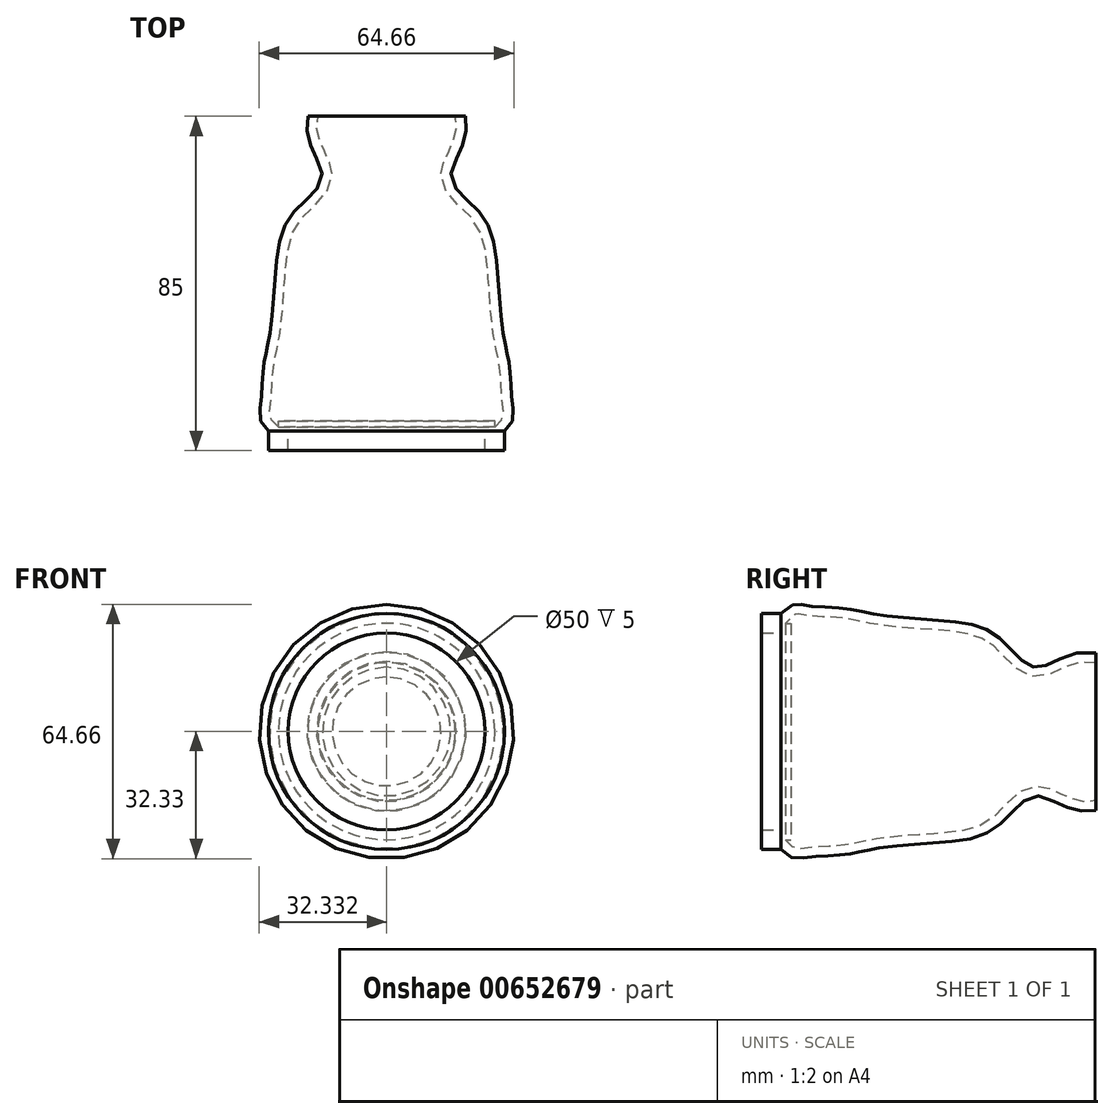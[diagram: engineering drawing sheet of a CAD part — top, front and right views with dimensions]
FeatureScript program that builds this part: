
annotation { "Feature Type Name" : "Feature", "Feature Type Description" : "" }
export const myFeature = defineFeature(function(context is Context, id is Id, definition is map)
    precondition{}
    {
        {
            var Q0;
            Q0=qCreatedBy(makeId("Top.planeOp"),FACE);
            var sketch = newSketch(context, id + "F0", { "sketchPlane" : qUnion([Q0])});
            skLineSegment(sketch, "E0", {"start": v(30.91, 63.74) * mm, "end": v(10.91, 63.74) * mm});
            skLineSegment(sketch, "E1", {"start": v(10.91, 63.74) * mm, "end": v(10.91, -16.26) * mm});
            skLineSegment(sketch, "E2", {"start": v(10.91, -16.26) * mm, "end": v(35.91, -16.26) * mm});
            skLineSegment(sketch, "E3", {"start": v(35.91, -16.26) * mm, "end": v(35.91, -21.26) * mm});
            skLineSegment(sketch, "E4", {"start": v(35.91, -21.26) * mm, "end": v(40.91, -21.26) * mm});
            skLineSegment(sketch, "E5", {"start": v(40.91, -21.26) * mm, "end": v(40.91, -16.26) * mm});
            skFitSpline(sketch, "E6", {"points": [v(30.91, 63.74) * mm, v(27.26, 48.32) * mm, v(35.19, 38.51) * mm, v(39.15, 23.98) * mm, v(40.66, 7.76) * mm, v(42.17, 0) * mm, v(42.93, -9.98) * mm, v(40.91, -16.26) * mm], "startDerivative": vector(27.61, -121.38) * mm, "endDerivative": vector(-85.08, -81.34) * mm});
            skSolve(sketch);
        }
        {
            var Q0;
            Q0 = qSketchRegion(id + "F0", true);
            var Q1;
            Q1=sQuery(id+"F0.wireOp",EDGE,"E1");
            revolve(context, id + "F1", {"surfaceOperationType" : NewSurfaceOperationType.NEW, "entities" : qUnion([Q0]), "axis" : qUnion([Q1]), "revolveType" : RevolveType.FULL});
        }
        {
            var Q0;
            Q0=makeQuery(id+"F1.opRevolve","SWEPT_FACE",FACE,{"disambiguationData":[OSD([sQuery(id+"F0.wireOp",EDGE,"E0")])]});
            shell(context, id + "F2", {"entities" : qUnion([Q0]), "thickness" : 2.5 * mm});
        }
    });
